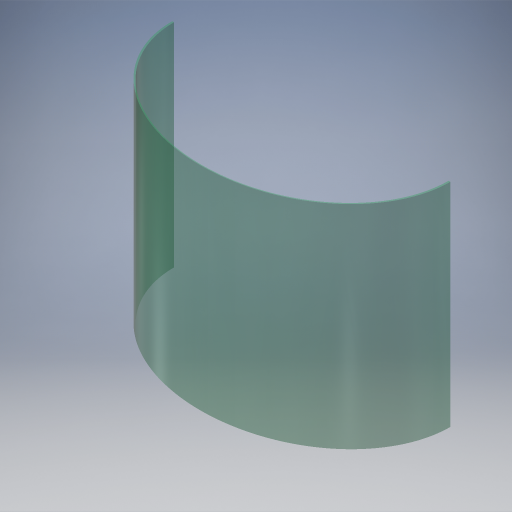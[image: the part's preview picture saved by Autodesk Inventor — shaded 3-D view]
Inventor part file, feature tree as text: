
AUTODESK INVENTOR PART (.ipt)
format: ipt  version: 2024.3 (Build 283343000, 343)  size: 284,672 bytes
history: native  units: mm
features: extrude x1
ambient origin geometry x8: Origin, YZ Plane, XZ Plane, XY Plane, X Axis, Y Axis, Z Axis, Center Point
bodies: Body1 (feature_tree)
feature tree (1):
  extrude  "Extrusion3"  Depth=300.0mm
